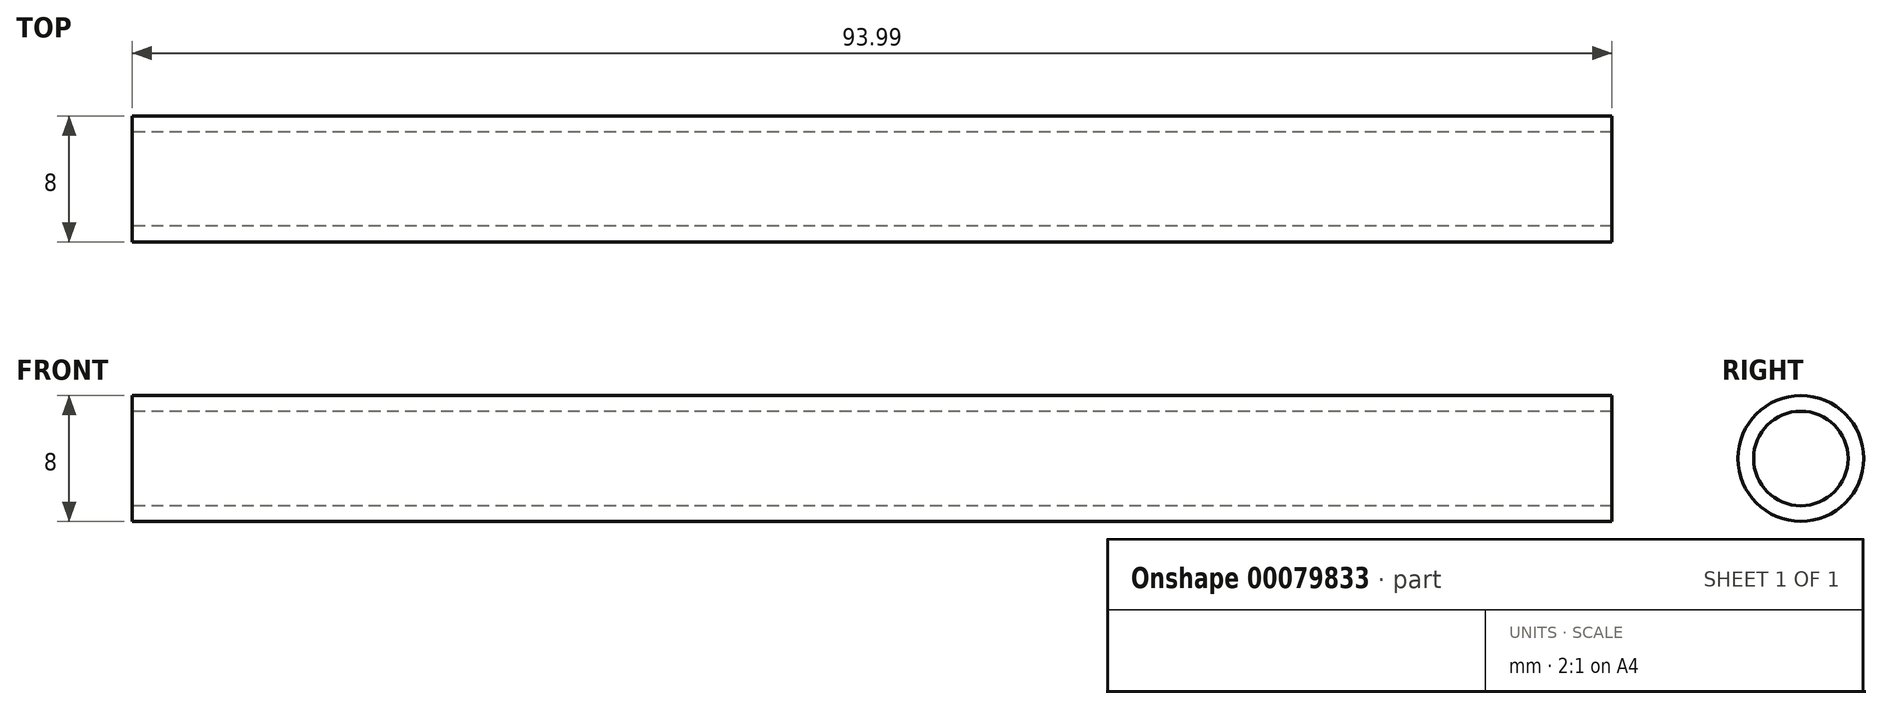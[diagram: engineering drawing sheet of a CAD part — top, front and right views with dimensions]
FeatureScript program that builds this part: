
annotation { "Feature Type Name" : "Feature", "Feature Type Description" : "" }
export const myFeature = defineFeature(function(context is Context, id is Id, definition is map)
    precondition{}
    {
        {
            var Q0;
            Q0=qCreatedBy(makeId("Front.planeOp"),FACE);
            var sketch = newSketch(context, id + "F0", { "sketchPlane" : qUnion([Q0])});
            skLineSegment(sketch, "E0", {"start": v(0, 0) * mm, "end": v(94, 0) * mm});
            skLineSegment(sketch, "E1", {"start": v(0, 0) * mm, "end": v(0, 4) * mm});
            skLineSegment(sketch, "E2", {"start": v(94, 0) * mm, "end": v(93.99, 4) * mm});
            skLineSegment(sketch, "E3", {"start": v(0, 4) * mm, "end": v(93.99, 4) * mm});
            skSolve(sketch);
        }
        {
            var Q0;
            Q0=qCreatedBy(makeId("Front.planeOp"),FACE);
            var sketch = newSketch(context, id + "F2", { "sketchPlane" : qUnion([Q0])});
            skLineSegment(sketch, "E4", {"start": v(-47.75, 0) * mm, "end": v(127.43, 0) * mm});
            skSolve(sketch);
        }
        {
            var Q0;
            Q0 = qSketchRegion(id + "F0", true);
            var Q1;
            Q1 = qBodyType(qCreatedBy(id + "F2" ,EDGE), BodyType.WIRE);
            revolve(context, id + "F3", {"entities" : qUnion([Q0]), "axis" : qUnion([Q1]), "revolveType" : RevolveType.FULL});
        }
        {
            var Q0;
            Q0=makeQuery(id+"F3.opRevolve","SWEPT_FACE",FACE,{"disambiguationData":[OSD([sQuery(id+"F0.wireOp",EDGE,"E2")])]});
            var Q1;
            Q1=makeQuery(id+"F3.opRevolve","SWEPT_FACE",FACE,{"disambiguationData":[OSD([sQuery(id+"F0.wireOp",EDGE,"E1")])]});
            shell(context, id + "F1", {"entities" : qUnion([Q0, Q1]), "thickness" : 1 * mm});
        }
    });
